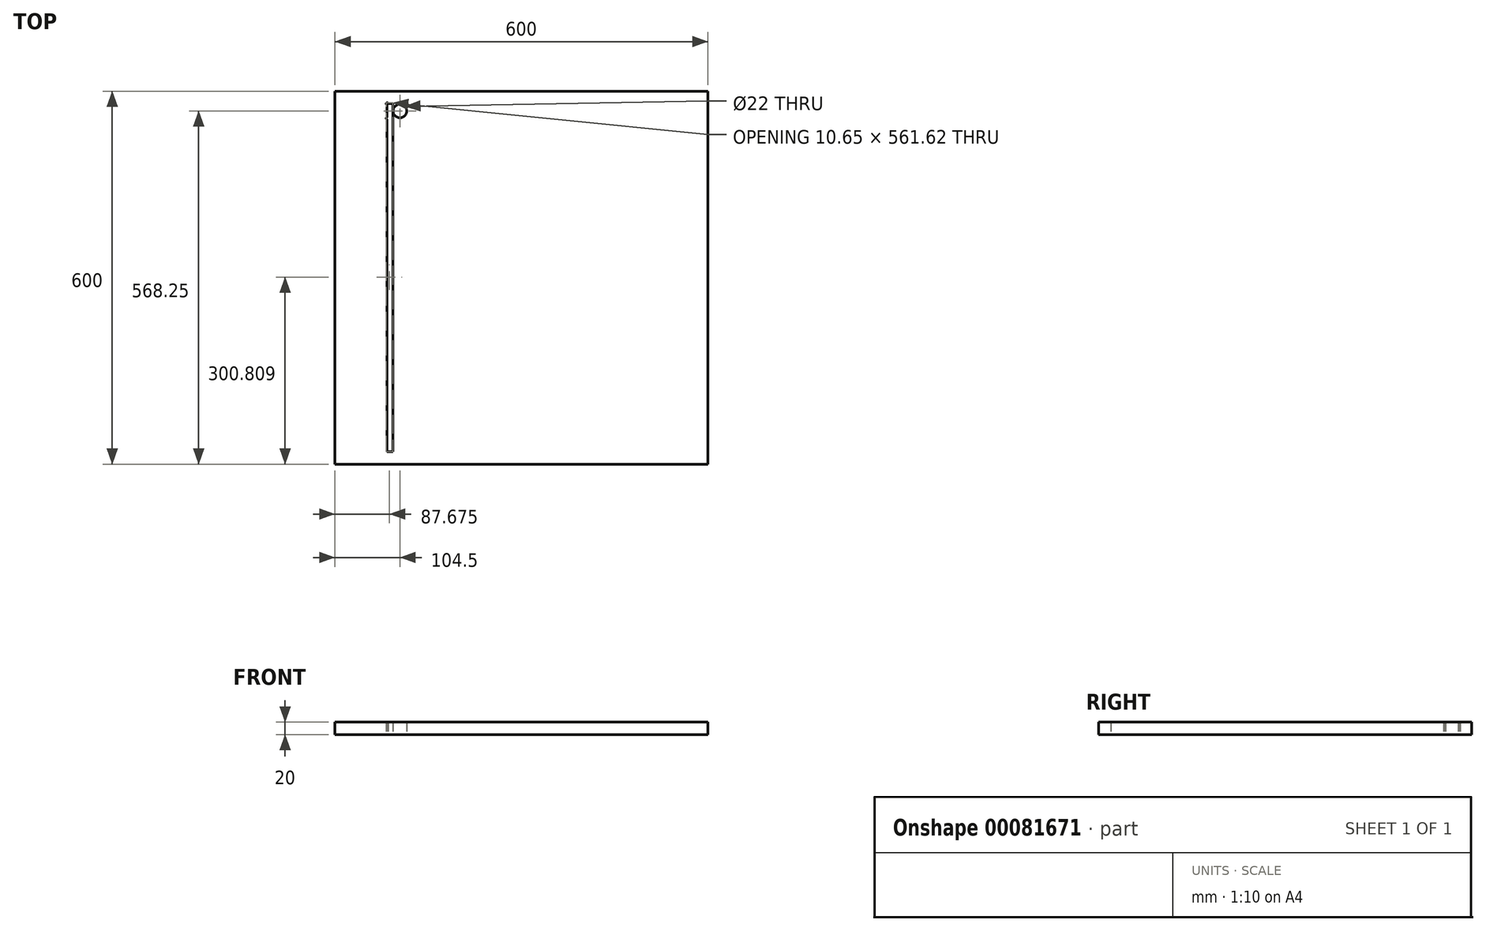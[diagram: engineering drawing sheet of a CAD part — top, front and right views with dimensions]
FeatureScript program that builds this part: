
annotation { "Feature Type Name" : "Feature", "Feature Type Description" : "" }
export const myFeature = defineFeature(function(context is Context, id is Id, definition is map)
    precondition{}
    {
        {
            var Q0;
            Q0=qCreatedBy(makeId("Top.planeOp"),FACE);
            var sketch = newSketch(context, id + "F0", { "sketchPlane" : qUnion([Q0])});
            skLineSegment(sketch, "E0.bottom", {"start": v(300, -300) * mm, "end": v(-300, -300) * mm});
            skLineSegment(sketch, "E0.top", {"start": v(300, 300) * mm, "end": v(-300, 300) * mm});
            skLineSegment(sketch, "E0.left", {"start": v(300, -300) * mm, "end": v(300, 300) * mm});
            skLineSegment(sketch, "E0.right", {"start": v(-300, -300) * mm, "end": v(-300, 300) * mm});
            skPoint(sketch, "E0.middle", {"position": v(0, 0) * mm});
            skLineSegment(sketch, "E1.bottom", {"start": v(-216, 300) * mm, "end": v(216, 300) * mm});
            skLineSegment(sketch, "E1.top", {"start": v(-216, -300) * mm, "end": v(216, -300) * mm});
            skLineSegment(sketch, "E1.left", {"start": v(-216, 300) * mm, "end": v(-216, -300) * mm});
            skLineSegment(sketch, "E1.right", {"start": v(216, 300) * mm, "end": v(216, -300) * mm});
            skLineSegment(sketch, "E2", {"start": v(-300, 300) * mm, "end": v(-216, 300) * mm});
            skLineSegment(sketch, "E3", {"start": v(216, 300) * mm, "end": v(300, 300) * mm});
            skLineSegment(sketch, "E4", {"start": v(-300, 300) * mm, "end": v(-300, 280) * mm});
            skLineSegment(sketch, "E5", {"start": v(-300, 280) * mm, "end": v(300, 280) * mm});
            skLineSegment(sketch, "E6", {"start": v(-300, -300) * mm, "end": v(-300, -280) * mm});
            skLineSegment(sketch, "E7", {"start": v(-300, -280) * mm, "end": v(216, -280) * mm});
            skPoint(sketch, "E8", {"position": v(-216, 280) * mm});
            skPoint(sketch, "E9", {"position": v(216, 280) * mm});
            skPoint(sketch, "E10", {"position": v(-216, -280) * mm});
            skPoint(sketch, "E11", {"position": v(216, -280) * mm});
            skLineSegment(sketch, "E12", {"start": v(216, -280) * mm, "end": v(300, -280) * mm});
            skLineSegment(sketch, "E13", {"start": v(-216, 280) * mm, "end": v(-216, 256.5) * mm});
            skLineSegment(sketch, "E14", {"start": v(216, 280) * mm, "end": v(216, 256.5) * mm});
            skLineSegment(sketch, "E15", {"start": v(-216, 268.25) * mm, "end": v(216, 268.25) * mm});
            skLineSegment(sketch, "E16.bottom", {"start": v(-216, 280) * mm, "end": v(-207, 280) * mm});
            skLineSegment(sketch, "E16.top", {"start": v(-216, -300) * mm, "end": v(-207, -300) * mm});
            skLineSegment(sketch, "E16.left", {"start": v(-216, 280) * mm, "end": v(-216, -300) * mm});
            skLineSegment(sketch, "E16.right", {"start": v(-207, 280) * mm, "end": v(-207, -300) * mm});
            skLineSegment(sketch, "E17", {"start": v(-207, 268.25) * mm, "end": v(-195.5, 268.25) * mm});
            skCircle(sketch, "E18", {"center": v(-195.5, 268.25) * mm, "radius": 11 * mm});
            skSolve(sketch);
        }
        {
            var Q0;
            Q0 = qSketchRegion(id + "F0", true);
            var Q1;
            {var subQ1=sQuery(id+"F0.wireOp",EDGE,"E14");var subQ6=sQuery(id+"F0.wireOp",EDGE,"E1.right");var subQ10=makeQuery(id+"F0.imprint","INTERSECT",VERTEX,{"derivedFrom":[subQ6,subQ1]});Q1=makeQuery(id+"F0.imprint","IMPRINT",FACE,{"disambiguationData":[TD([[makeQuery(id+"F0.imprint","IMPRINT",EDGE,{"disambiguationData":[TD([[subQ10,1.0]])],"derivedFrom":subQ1}),-1.0]])]});}
            var Q2;
            {var subQ4=sQuery(id+"F0.wireOp",EDGE,"E15");var subQ6=sQuery(id+"F0.wireOp",EDGE,"E14");var subQ7=makeQuery(id+"F0.imprint","INTERSECT",VERTEX,{"derivedFrom":[subQ6,subQ4]});Q2=makeQuery(id+"F0.imprint","IMPRINT",FACE,{"disambiguationData":[TD([[makeQuery(id+"F0.imprint","IMPRINT",EDGE,{"disambiguationData":[TD([[subQ7,1.0]])],"derivedFrom":subQ4}),1.0]])]});}
            var Q3;
            {var subQ0=sQuery(id+"F0.wireOp",EDGE,"E17");var subQ1=sQuery(id+"F0.wireOp",EDGE,"E15");var subQ2=makeQuery(id+"F0.imprint","INTERSECT",VERTEX,{"derivedFrom":[subQ1,subQ0]});Q3=makeQuery(id+"F0.imprint","IMPRINT",FACE,{"disambiguationData":[TD([[makeQuery(id+"F0.imprint","IMPRINT",EDGE,{"disambiguationData":[TD([[subQ2,-1.0]])],"derivedFrom":subQ1}),1.0]])]});}
            var Q4;
            {var subQ0=sQuery(id+"F0.wireOp",EDGE,"E17");var subQ1=sQuery(id+"F0.wireOp",EDGE,"E15");var subQ2=makeQuery(id+"F0.imprint","INTERSECT",VERTEX,{"derivedFrom":[subQ1,subQ0]});Q4=makeQuery(id+"F0.imprint","IMPRINT",FACE,{"disambiguationData":[TD([[makeQuery(id+"F0.imprint","IMPRINT",EDGE,{"disambiguationData":[TD([[subQ2,-1.0]])],"derivedFrom":subQ1}),-1.0]])]});}
            var Q5;
            {var subQ0=sQuery(id+"F0.wireOp",EDGE,"E16.left");var subQ1=makeQuery(id+"F0.imprint","IMPRINT",VERTEX,{"derivedFrom":subQ0});Q5=makeQuery(id+"F0.imprint","IMPRINT",FACE,{"disambiguationData":[TD([[makeQuery(id+"F0.imprint","IMPRINT",EDGE,{"disambiguationData":[TD([[subQ1,1.0]])],"derivedFrom":subQ0}),1.0]])]});}
            var Q6;
            {var subQ5=sQuery(id+"F0.wireOp",EDGE,"E16.bottom");Q6=makeQuery(id+"F0.imprint","IMPRINT",FACE,{"disambiguationData":[TD([[makeQuery(id+"F0.imprint","IMPRINT",EDGE,{"derivedFrom":subQ5}),-1.0]])]});}
            extrude(context, id + "F1", {"entities" : qUnion([Q0, Q1, Q2, Q3, Q4, Q5, Q6]), "depth" : 20 * mm});
        }
        {
            var Q0;
            Q0=sQuery(id+"F0.wireOp",VERTEX,"E8");
            var Q1;
            Q1=sQuery(id+"F0.wireOp",VERTEX,"E13.end");
            var Q2;
            Q2=makeQuery(id+"F1.opExtrude","SWEPT_BODY",BODY,{"disambiguationData":[OSD([sQuery(id+"F0.wireOp",EDGE,"E0.bottom"),sQuery(id+"F0.wireOp",EDGE,"E0.left"),sQuery(id+"F0.wireOp",EDGE,"E0.right"),sQuery(id+"F0.wireOp",EDGE,"E1.bottom"),sQuery(id+"F0.wireOp",EDGE,"E1.top"),sQuery(id+"F0.wireOp",EDGE,"E2"),sQuery(id+"F0.wireOp",EDGE,"E3"),sQuery(id+"F0.wireOp",EDGE,"E4"),sQuery(id+"F0.wireOp",EDGE,"E6"),sQuery(id+"F0.wireOp",EDGE,"E16.top")])]});
            hole(context, id + "F2", {"style" : HoleStyle.SIMPLE, "endStyle" : HoleEndStyle.THROUGH, "oppositeDirection" : true, "standardTappedOrClearance" : lookupTablePath({ "standard" : "ISO", "fit" : "Normal", "size" : "M3", "type" : "Clearance" }), "standardBlindInLast" : lookupTablePath({ "fit" : "Standard", "standard" : "ISO", "size" : "M3", "type" : "Clearance" }), "holeDiameter" : 3.3 * mm, "locations" : qUnion([Q0, Q1]), "scope" : qUnion([Q2]), "isTappedThrough" : true});
        }
        {
            var Q0;
            Q0=sQuery(id+"F0.wireOp",VERTEX,"E17.end");
            var Q1;
            Q1=makeQuery(id+"F1.opExtrude","SWEPT_BODY",BODY,{"disambiguationData":[OSD([sQuery(id+"F0.wireOp",EDGE,"E0.bottom"),sQuery(id+"F0.wireOp",EDGE,"E0.left"),sQuery(id+"F0.wireOp",EDGE,"E0.right"),sQuery(id+"F0.wireOp",EDGE,"E1.bottom"),sQuery(id+"F0.wireOp",EDGE,"E1.top"),sQuery(id+"F0.wireOp",EDGE,"E2"),sQuery(id+"F0.wireOp",EDGE,"E3"),sQuery(id+"F0.wireOp",EDGE,"E4"),sQuery(id+"F0.wireOp",EDGE,"E6"),sQuery(id+"F0.wireOp",EDGE,"E16.top")])]});
            hole(context, id + "F3", {"style" : HoleStyle.SIMPLE, "endStyle" : HoleEndStyle.THROUGH, "oppositeDirection" : true, "standardTappedOrClearance" : lookupTablePath({ "standard" : "ISO", "fit" : "Normal", "size" : "M8", "type" : "Clearance" }), "standardBlindInLast" : lookupTablePath({ "fit" : "Standard", "standard" : "ISO", "size" : "M8", "type" : "Clearance" }), "holeDiameter" : 8.8 * mm, "locations" : qUnion([Q0]), "scope" : qUnion([Q1]), "isTappedThrough" : true});
        }
    });
